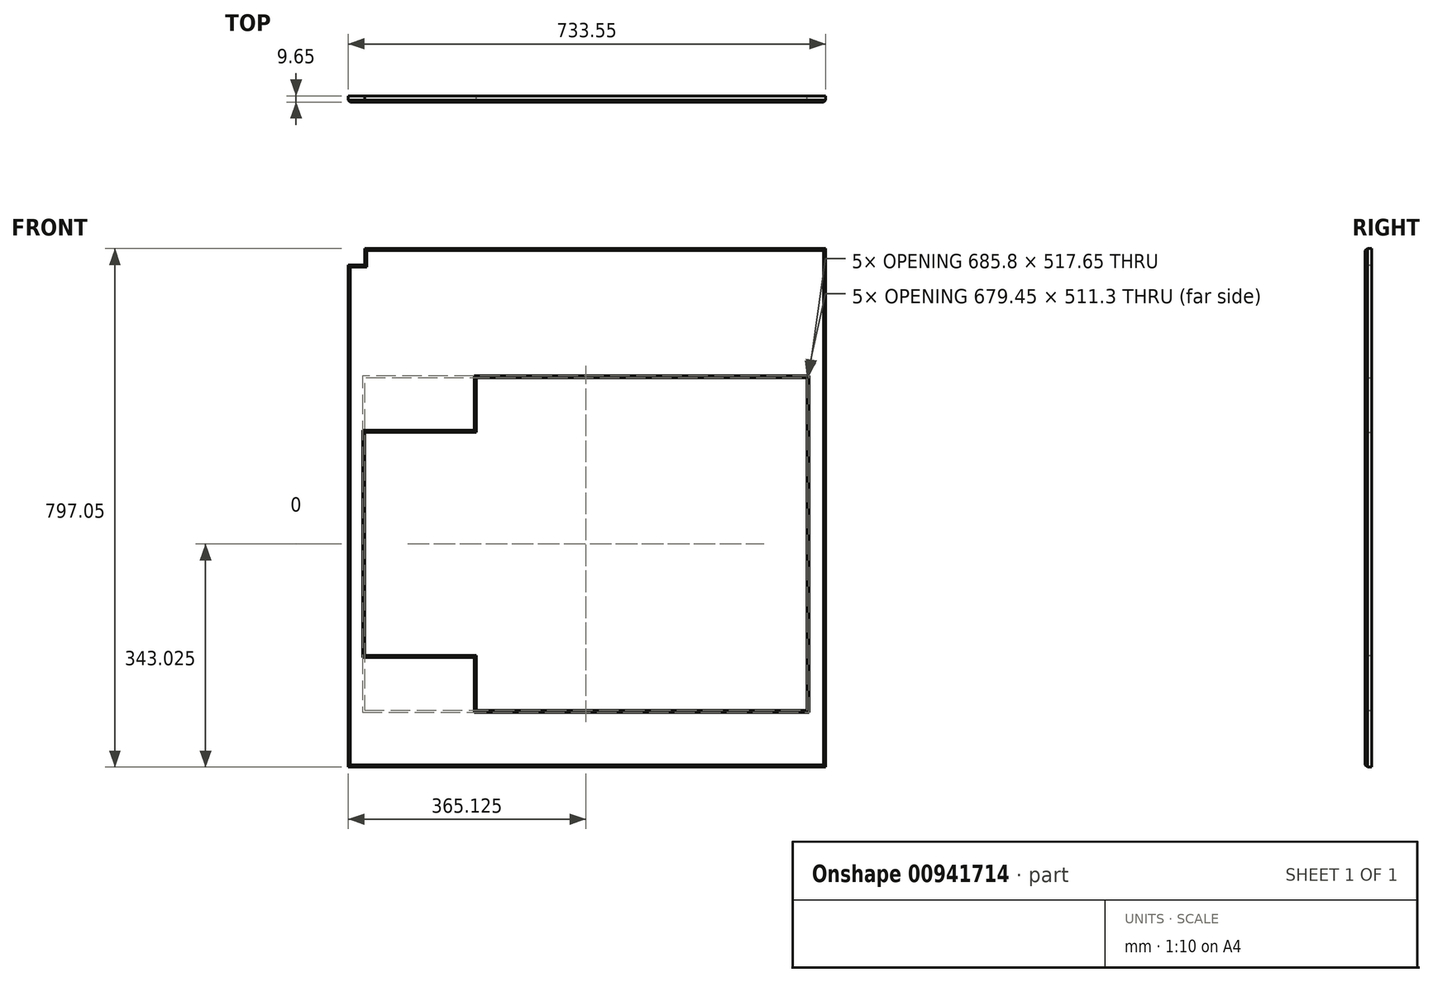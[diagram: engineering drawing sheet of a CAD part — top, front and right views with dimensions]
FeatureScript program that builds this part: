
annotation { "Feature Type Name" : "Feature", "Feature Type Description" : "" }
export const myFeature = defineFeature(function(context is Context, id is Id, definition is map)
    precondition{}
    {
        {
            var Q0;
            Q0=qCreatedBy(makeId("Front.planeOp"),FACE);
            var sketch = newSketch(context, id + "F0", { "sketchPlane" : qUnion([Q0])});
            skLineSegment(sketch, "E0.top", {"start": v(-447.8, -308.16) * mm, "end": v(285.75, -308.16) * mm});
            skLineSegment(sketch, "E0.right", {"start": v(285.75, 488.89) * mm, "end": v(285.75, -308.16) * mm});
            skLineSegment(sketch, "E1.top", {"start": v(-422.4, 206.19) * mm, "end": v(-250.95, 206.19) * mm});
            skLineSegment(sketch, "E1.right", {"start": v(-250.95, 290.52) * mm, "end": v(-250.95, 206.19) * mm});
            skLineSegment(sketch, "E2.bottom", {"start": v(-422.4, -136.71) * mm, "end": v(-250.95, -136.71) * mm});
            skLineSegment(sketch, "E2.right", {"start": v(-250.95, -136.71) * mm, "end": v(-250.95, -220.79) * mm});
            skLineSegment(sketch, "E3.bottom", {"start": v(-250.95, 290.52) * mm, "end": v(257.05, 290.52) * mm});
            skLineSegment(sketch, "E3.top", {"start": v(-250.95, -220.79) * mm, "end": v(257.05, -220.79) * mm});
            skLineSegment(sketch, "E3.right", {"start": v(257.05, 290.52) * mm, "end": v(257.05, -220.79) * mm});
            skLineSegment(sketch, "E4.left", {"start": v(-422.4, 206.19) * mm, "end": v(-422.4, -136.71) * mm});
            skLineSegment(sketch, "E5.top", {"start": v(-447.8, 463.49) * mm, "end": v(-422.4, 463.49) * mm});
            skLineSegment(sketch, "E5.right", {"start": v(-422.4, 488.89) * mm, "end": v(-422.4, 463.49) * mm});
            skLineSegment(sketch, "E6", {"start": v(-447.8, 463.49) * mm, "end": v(-447.8, -308.16) * mm});
            skLineSegment(sketch, "E7", {"start": v(-422.4, 488.89) * mm, "end": v(285.75, 488.89) * mm});
            skSolve(sketch);
        }
        {
            var Q0;
            Q0=makeQuery(id+"F0.imprint","IMPRINT",FACE,{"disambiguationData":[TD([[makeQuery(id+"F0.imprint","IMPRINT",EDGE,{"derivedFrom":sQuery(id+"F0.wireOp",EDGE,"E0.top")}),1.0]])]});
            extrude(context, id + "F1", {"entities" : qUnion([Q0]), "depth" : 9.65 * mm, "offsetDistance" : 25.4 * mm});
        }
        {
            var Q0;
            Q0=makeQuery(id+"F1.opExtrude","CAP_FACE",FACE,{"disambiguationData":[OSD([sQuery(id+"F0.wireOp",EDGE,"E0.top"),sQuery(id+"F0.wireOp",EDGE,"E0.right"),sQuery(id+"F0.wireOp",EDGE,"E1.right"),sQuery(id+"F0.wireOp",EDGE,"E2.right"),sQuery(id+"F0.wireOp",EDGE,"E3.bottom"),sQuery(id+"F0.wireOp",EDGE,"E3.top"),sQuery(id+"F0.wireOp",EDGE,"E3.right"),sQuery(id+"F0.wireOp",EDGE,"E1.top"),sQuery(id+"F0.wireOp",EDGE,"E2.bottom"),sQuery(id+"F0.wireOp",EDGE,"E4.left"),sQuery(id+"F0.wireOp",EDGE,"E5.top"),sQuery(id+"F0.wireOp",EDGE,"E5.right"),sQuery(id+"F0.wireOp",EDGE,"E6"),sQuery(id+"F0.wireOp",EDGE,"E7")])],"isStart":false});
            chamfer(context, id + "F2", {"entities" : qUnion([Q0]), "width" : 3.17 * mm, "tangentPropagation" : true});
        }
    });
